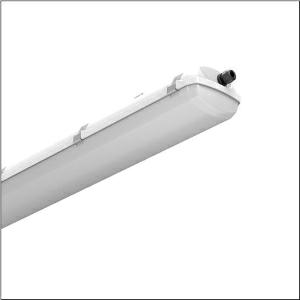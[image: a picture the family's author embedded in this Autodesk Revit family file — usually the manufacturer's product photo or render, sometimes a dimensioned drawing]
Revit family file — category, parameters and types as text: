
# Revit family: monsun_r__ex_51fxb17p4d0a_83d7
name_source: partatom
category: Lighting Fixtures
units: mm (PartAtom-declared; Revit-internal decimal feet)

## family parameters
Cut with Voids When Loaded = No
Host = Face
Light Source = No
Part Type = Normal
Room Calculation Point = No
Round Connector Dimension = Use Diameter
Shared = No

## types (1)
- Monsun® Ex (1 x LED, 17900 lm, 116.3 W, 4000K)
    Apparent Load = 116 VA
    CIE Flux Codes = 61 86 97 98 100
    Color Rendering = 80
    Color Temperature = 4000K
    Default Elevation = 1800 mm
    Description = Monsun® Ex, damp-proof luminaire, primary optical cover: cover, of PC, UV-stabilised, opal, light emission: direct distribution, primary light characteristic: symmetric, installation type: surface-mounted, LED, rated luminous flux: 17.900lm, luminous efficacy: 154lm/W, light colour: 840, colour temperature: 4000K, control gear: ECG, with terminal, 3-pole, max. 2.5mm², through-wiring: 5x 2.5mm², mains connection: 220..240V, AC, 50/60Hz, rated input power: 116W, housing, of PC, light grey (RAL 7035), incl. blind plug, incl. 1x Ex cable gland M20 for cable diameter 7..12mm with sealing, length: 1.580mm, width: 155mm, height: 105mm, clip for enclosure, of stainless steel, protection rating (complete): IP66, insulation class (complete): insulation class I (protective earthing), certification: CE, explosion class: zone2,22 II 3G Ex nR IIC T6 GC, II 3D Ex tc IIIC T80°C Dc, impact resistance: IK10, permissible operating ambient temperature: -20..+40°C, LABS conformity tested according to VDMA 24364:2018-05, contact your sales advisor before using the luminaires in applications with unclear chemical exposure, large temperature fluctuations or condensation-forming humidity, packaging unit: 1 piece
    Height = 105 mm
    Lamp = 1 x LED
    Lamp Light Flux = 17900 lm
    Lamp Power = 116.3 W
    Lamp count = 1
    Length = 1580 mm
    Luminous efficacy = 154 lm/W
    Manufacturer = Siteco
    ModVariant = No
    Model = 51FXB17P4D0A
    Mounting Place = Ceiling
    Mounting Type = Surface mounted
    Number of Poles = 1
    OnlyDefault = Yes
    Power Factor = 1
    Product Name = Monsun® Ex
    Product group = damp-proof luminaire
    ProductGroupID = 301
    Protection Class = Protection class I
    Protection Degree = IP 66
    RLX_Detail_Level = 1
    RLX_Emergency_Light_Flux = 0 lm
    RLX_Emergency_Type = 0
    RLX_Emergency_Type_DB = No
    RlxData = <blob elided: 41833 chars, md5=ee7afd4f>
    Socket = socket
    Standby Power = 0 W
    System Light Flux = 17900 lm
    System Power = 116 W
    Type Comments = Product without accessories
    Type Image = l_1258882.jpg
    URL = http://relux.com
    VarID = ---
    Voltage = 0 V
    Weight = 0.00 kg
    Width = 155 mm

## geometry (parser evidence)
native form markers: Blend x4, Sweep x9
no freeform markers — native parametric forms only
